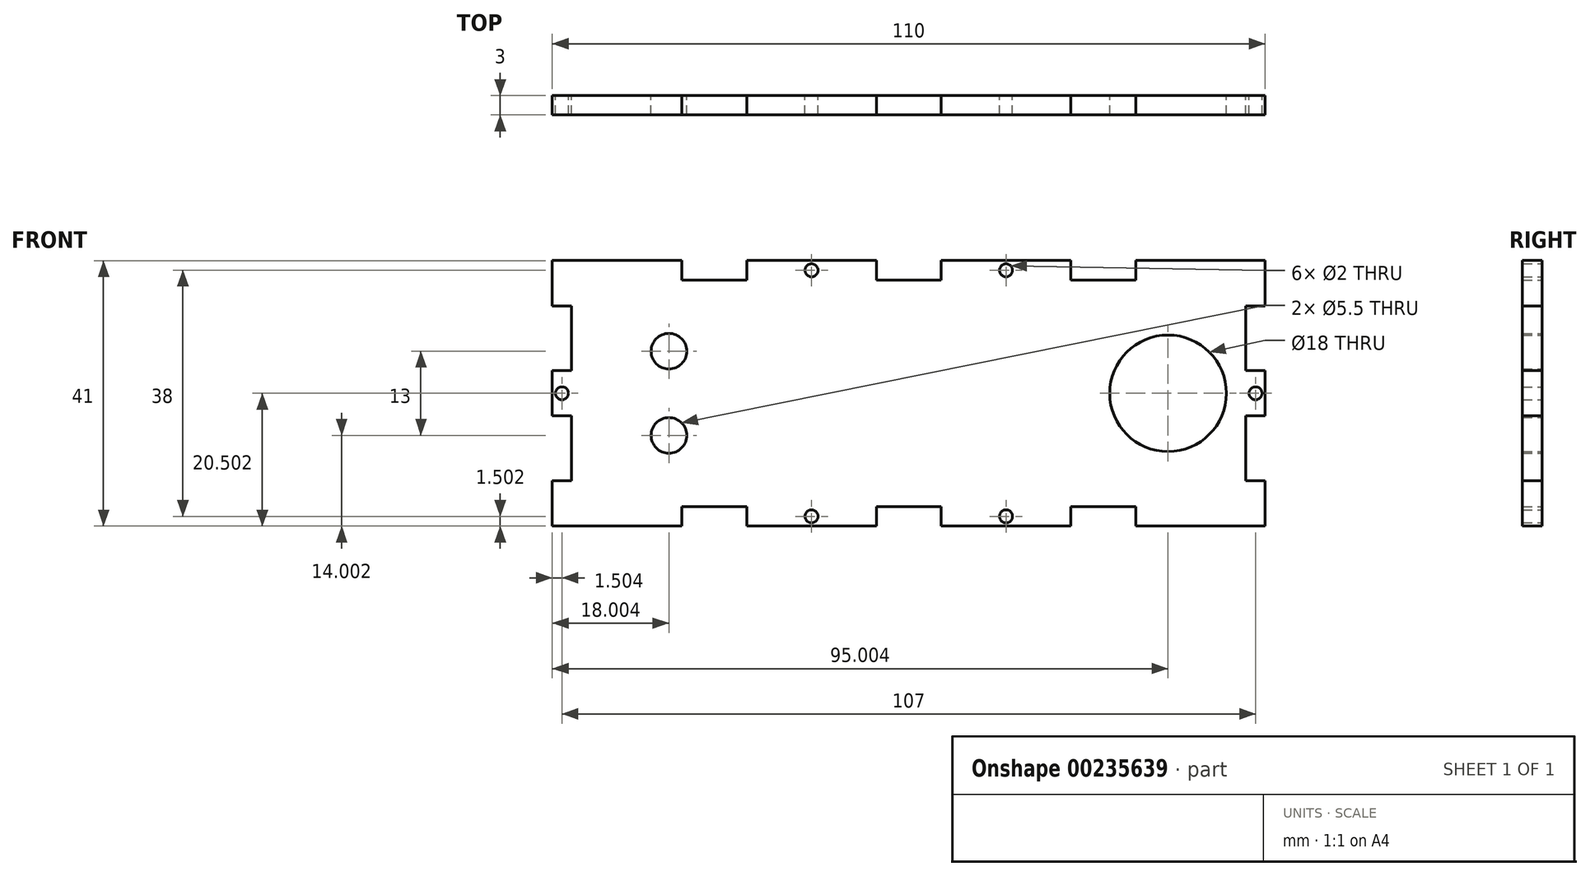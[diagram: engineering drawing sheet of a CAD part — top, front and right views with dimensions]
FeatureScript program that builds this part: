
annotation { "Feature Type Name" : "Feature", "Feature Type Description" : "" }
export const myFeature = defineFeature(function(context is Context, id is Id, definition is map)
    precondition{}
    {
        {
            var Q0;
            Q0=qCreatedBy(makeId("Front.planeOp"),FACE);
            var sketch = newSketch(context, id + "F0", { "sketchPlane" : qUnion([Q0])});
            skLineSegment(sketch, "E0", {"start": v(54.92, -20.79) * mm, "end": v(54.92, -13.79) * mm});
            skLineSegment(sketch, "E1", {"start": v(54.92, -13.79) * mm, "end": v(51.92, -13.79) * mm});
            skLineSegment(sketch, "E2", {"start": v(51.92, -13.79) * mm, "end": v(51.92, -3.79) * mm});
            skLineSegment(sketch, "E3", {"start": v(51.92, -3.79) * mm, "end": v(54.92, -3.79) * mm});
            skLineSegment(sketch, "E4", {"start": v(54.92, -3.79) * mm, "end": v(54.92, 3.21) * mm});
            skLineSegment(sketch, "E5", {"start": v(54.92, 3.21) * mm, "end": v(51.92, 3.21) * mm});
            skLineSegment(sketch, "E6", {"start": v(51.92, 3.21) * mm, "end": v(51.92, 13.21) * mm});
            skLineSegment(sketch, "E7", {"start": v(51.92, 13.21) * mm, "end": v(54.92, 13.21) * mm});
            skLineSegment(sketch, "E8", {"start": v(54.92, 13.21) * mm, "end": v(54.92, 20.21) * mm});
            skLineSegment(sketch, "E9", {"start": v(54.92, 20.21) * mm, "end": v(34.92, 20.21) * mm});
            skLineSegment(sketch, "E10", {"start": v(34.92, 20.21) * mm, "end": v(34.92, 17.21) * mm});
            skLineSegment(sketch, "E11", {"start": v(34.92, 17.21) * mm, "end": v(24.92, 17.21) * mm});
            skLineSegment(sketch, "E12", {"start": v(24.92, 17.21) * mm, "end": v(24.92, 20.21) * mm});
            skLineSegment(sketch, "E13", {"start": v(24.92, 20.21) * mm, "end": v(4.92, 20.21) * mm});
            skLineSegment(sketch, "E14", {"start": v(4.92, 20.21) * mm, "end": v(4.92, 17.21) * mm});
            skLineSegment(sketch, "E15", {"start": v(4.92, 17.21) * mm, "end": v(-0.08, 17.21) * mm});
            skLineSegment(sketch, "E16", {"start": v(54.92, -20.79) * mm, "end": v(34.92, -20.79) * mm});
            skLineSegment(sketch, "E17", {"start": v(34.92, -20.79) * mm, "end": v(34.92, -17.79) * mm});
            skLineSegment(sketch, "E18", {"start": v(34.92, -17.79) * mm, "end": v(24.92, -17.79) * mm});
            skLineSegment(sketch, "E19", {"start": v(24.92, -17.79) * mm, "end": v(24.92, -20.79) * mm});
            skLineSegment(sketch, "E20", {"start": v(24.92, -20.79) * mm, "end": v(4.92, -20.79) * mm});
            skLineSegment(sketch, "E21", {"start": v(4.92, -17.79) * mm, "end": v(-0.08, -17.79) * mm});
            skLineSegment(sketch, "E22", {"start": v(4.92, -17.79) * mm, "end": v(4.92, -20.79) * mm});
            skLineSegment(sketch, "E23", {"start": v(-0.08, 17.21) * mm, "end": v(-0.08, -17.79) * mm, "construction": true});
            skLineSegment(sketch, "E24.MirrorCS", {"start": v(-5.08, 17.21) * mm, "end": v(-0.08, 17.21) * mm});
            skLineSegment(sketch, "E25.MirrorCS", {"start": v(-5.08, -17.79) * mm, "end": v(-0.08, -17.79) * mm});
            skLineSegment(sketch, "E26.MirrorCS", {"start": v(-5.08, 20.21) * mm, "end": v(-5.08, 17.21) * mm});
            skLineSegment(sketch, "E27.MirrorCS", {"start": v(-5.08, -17.79) * mm, "end": v(-5.08, -20.79) * mm});
            skLineSegment(sketch, "E28.MirrorCS", {"start": v(-25.08, -17.79) * mm, "end": v(-25.08, -20.79) * mm});
            skLineSegment(sketch, "E29.MirrorCS", {"start": v(-25.08, 17.21) * mm, "end": v(-25.08, 20.21) * mm});
            skLineSegment(sketch, "E30.MirrorCS", {"start": v(-55.08, -13.79) * mm, "end": v(-52.08, -13.79) * mm});
            skLineSegment(sketch, "E31.MirrorCS", {"start": v(-35.08, -20.79) * mm, "end": v(-35.08, -17.79) * mm});
            skLineSegment(sketch, "E32.MirrorCS", {"start": v(-52.08, -3.79) * mm, "end": v(-55.08, -3.79) * mm});
            skLineSegment(sketch, "E33.MirrorCS", {"start": v(-55.08, 3.21) * mm, "end": v(-52.08, 3.21) * mm});
            skLineSegment(sketch, "E34.MirrorCS", {"start": v(-52.08, 13.21) * mm, "end": v(-55.08, 13.21) * mm});
            skLineSegment(sketch, "E35.MirrorCS", {"start": v(-35.08, 20.21) * mm, "end": v(-35.08, 17.21) * mm});
            skLineSegment(sketch, "E36.MirrorCS", {"start": v(-25.08, -20.79) * mm, "end": v(-5.08, -20.79) * mm});
            skLineSegment(sketch, "E37.MirrorCS", {"start": v(-55.08, -20.79) * mm, "end": v(-35.08, -20.79) * mm});
            skLineSegment(sketch, "E38.MirrorCS", {"start": v(-55.08, -3.79) * mm, "end": v(-55.08, 3.21) * mm});
            skLineSegment(sketch, "E39.MirrorCS", {"start": v(-55.08, -20.79) * mm, "end": v(-55.08, -13.79) * mm});
            skLineSegment(sketch, "E40.MirrorCS", {"start": v(-25.08, 20.21) * mm, "end": v(-5.08, 20.21) * mm});
            skLineSegment(sketch, "E41.MirrorCS", {"start": v(-35.08, -17.79) * mm, "end": v(-25.08, -17.79) * mm});
            skLineSegment(sketch, "E42.MirrorCS", {"start": v(-55.08, 20.21) * mm, "end": v(-35.08, 20.21) * mm});
            skLineSegment(sketch, "E43.MirrorCS", {"start": v(-55.08, 13.21) * mm, "end": v(-55.08, 20.21) * mm});
            skLineSegment(sketch, "E44.MirrorCS", {"start": v(-52.08, -13.79) * mm, "end": v(-52.08, -3.79) * mm});
            skLineSegment(sketch, "E45.MirrorCS", {"start": v(-35.08, 17.21) * mm, "end": v(-25.08, 17.21) * mm});
            skLineSegment(sketch, "E46.MirrorCS", {"start": v(-52.08, 3.21) * mm, "end": v(-52.08, 13.21) * mm});
            skPoint(sketch, "E47.centerSnap0", {"position": v(-53.58, 3.21) * mm});
            skPoint(sketch, "E47.centerSnap1", {"position": v(-55.08, -0.29) * mm});
            skPoint(sketch, "E48.centerSnap0", {"position": v(-15.08, -20.79) * mm});
            skPoint(sketch, "E48.centerSnap1", {"position": v(-25.08, -19.29) * mm});
            skPoint(sketch, "E49.centerSnap0", {"position": v(4.92, -19.29) * mm});
            skPoint(sketch, "E49.centerSnap1", {"position": v(14.92, -20.79) * mm});
            skPoint(sketch, "E50.centerSnap0", {"position": v(-5.08, 18.71) * mm});
            skPoint(sketch, "E50.centerSnap1", {"position": v(-15.08, 20.21) * mm});
            skCircle(sketch, "E51", {"center": v(-15.08, 18.71) * mm, "radius": 1 * mm});
            skCircle(sketch, "E52", {"center": v(53.42, -0.29) * mm, "radius": 1 * mm});
            skPoint(sketch, "E52.centerSnap0", {"position": v(54.92, -0.29) * mm});
            skPoint(sketch, "E52.centerSnap1", {"position": v(53.42, -3.79) * mm});
            skPoint(sketch, "E53.centerSnap0", {"position": v(4.92, 18.71) * mm});
            skPoint(sketch, "E53.centerSnap1", {"position": v(14.92, 20.21) * mm});
            skCircle(sketch, "E54", {"center": v(14.92, 18.71) * mm, "radius": 1 * mm});
            skPoint(sketch, "E54.centerSnap0", {"position": v(24.92, 18.71) * mm});
            skCircle(sketch, "E55", {"center": v(-53.58, -0.29) * mm, "radius": 1 * mm});
            skCircle(sketch, "E56", {"center": v(-15.08, -19.29) * mm, "radius": 1 * mm});
            skCircle(sketch, "E57", {"center": v(14.92, -19.29) * mm, "radius": 1 * mm});
            skCircle(sketch, "E58", {"center": v(39.92, -0.29) * mm, "radius": 9 * mm});
            skCircle(sketch, "E59", {"center": v(-37.08, -6.79) * mm, "radius": 2.75 * mm});
            skCircle(sketch, "E60", {"center": v(-37.08, 6.21) * mm, "radius": 2.75 * mm});
            skSolve(sketch);
        }
        {
            var Q0;
            Q0 = qSketchRegion(id + "F0", true);
            extrude(context, id + "F1", {"entities" : qUnion([Q0]), "depth" : 3 * mm});
        }
    });
